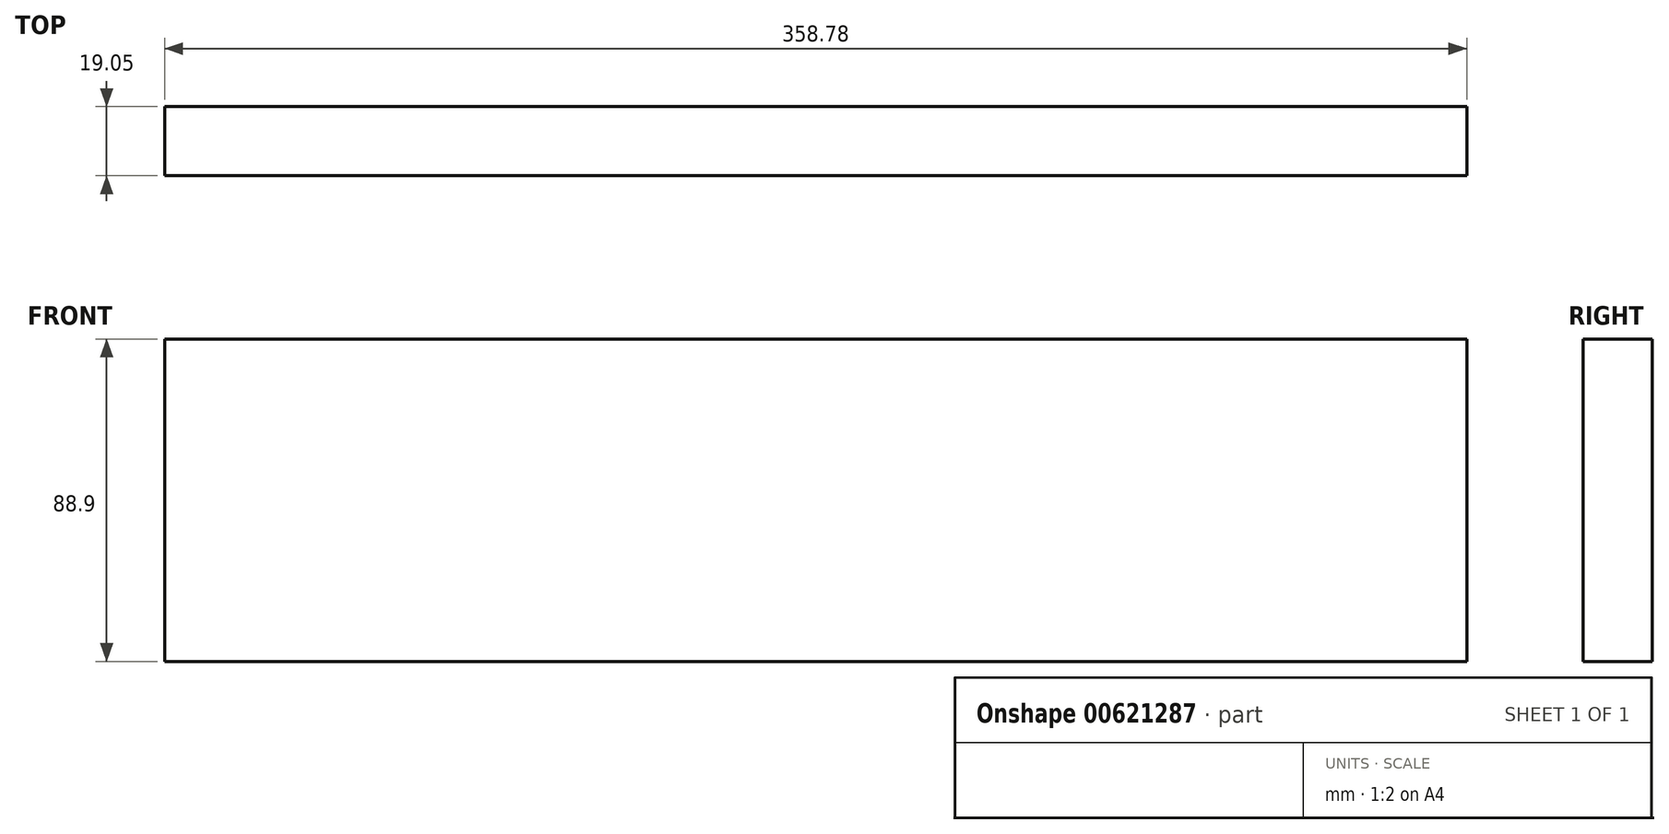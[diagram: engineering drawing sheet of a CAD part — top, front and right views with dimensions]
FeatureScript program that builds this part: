
annotation { "Feature Type Name" : "Feature", "Feature Type Description" : "" }
export const myFeature = defineFeature(function(context is Context, id is Id, definition is map)
    precondition{}
    {
        {
            var Q0;
            Q0=qCreatedBy(makeId("Front.planeOp"),FACE);
            var sketch = newSketch(context, id + "F0", { "sketchPlane" : qUnion([Q0])});
            skLineSegment(sketch, "E0.bottom", {"start": v(179.39, 44.45) * mm, "end": v(-179.39, 44.45) * mm});
            skLineSegment(sketch, "E0.top", {"start": v(179.39, -44.45) * mm, "end": v(-179.39, -44.45) * mm});
            skLineSegment(sketch, "E0.left", {"start": v(179.39, 44.45) * mm, "end": v(179.39, -44.45) * mm});
            skLineSegment(sketch, "E0.right", {"start": v(-179.39, 44.45) * mm, "end": v(-179.39, -44.45) * mm});
            skPoint(sketch, "E0.middle", {"position": v(0, 0) * mm});
            skSolve(sketch);
        }
        {
            var Q0;
            Q0=makeQuery(id+"F0.imprint","IMPRINT",FACE,{"disambiguationData":[TD([[makeQuery(id+"F0.imprint","IMPRINT",EDGE,{"derivedFrom":sQuery(id+"F0.wireOp",EDGE,"E0.bottom")}),1.0]])]});
            extrude(context, id + "F1", {"entities" : qUnion([Q0]), "depth" : 19.05 * mm, "offsetDistance" : 25.4 * mm});
        }
    });
